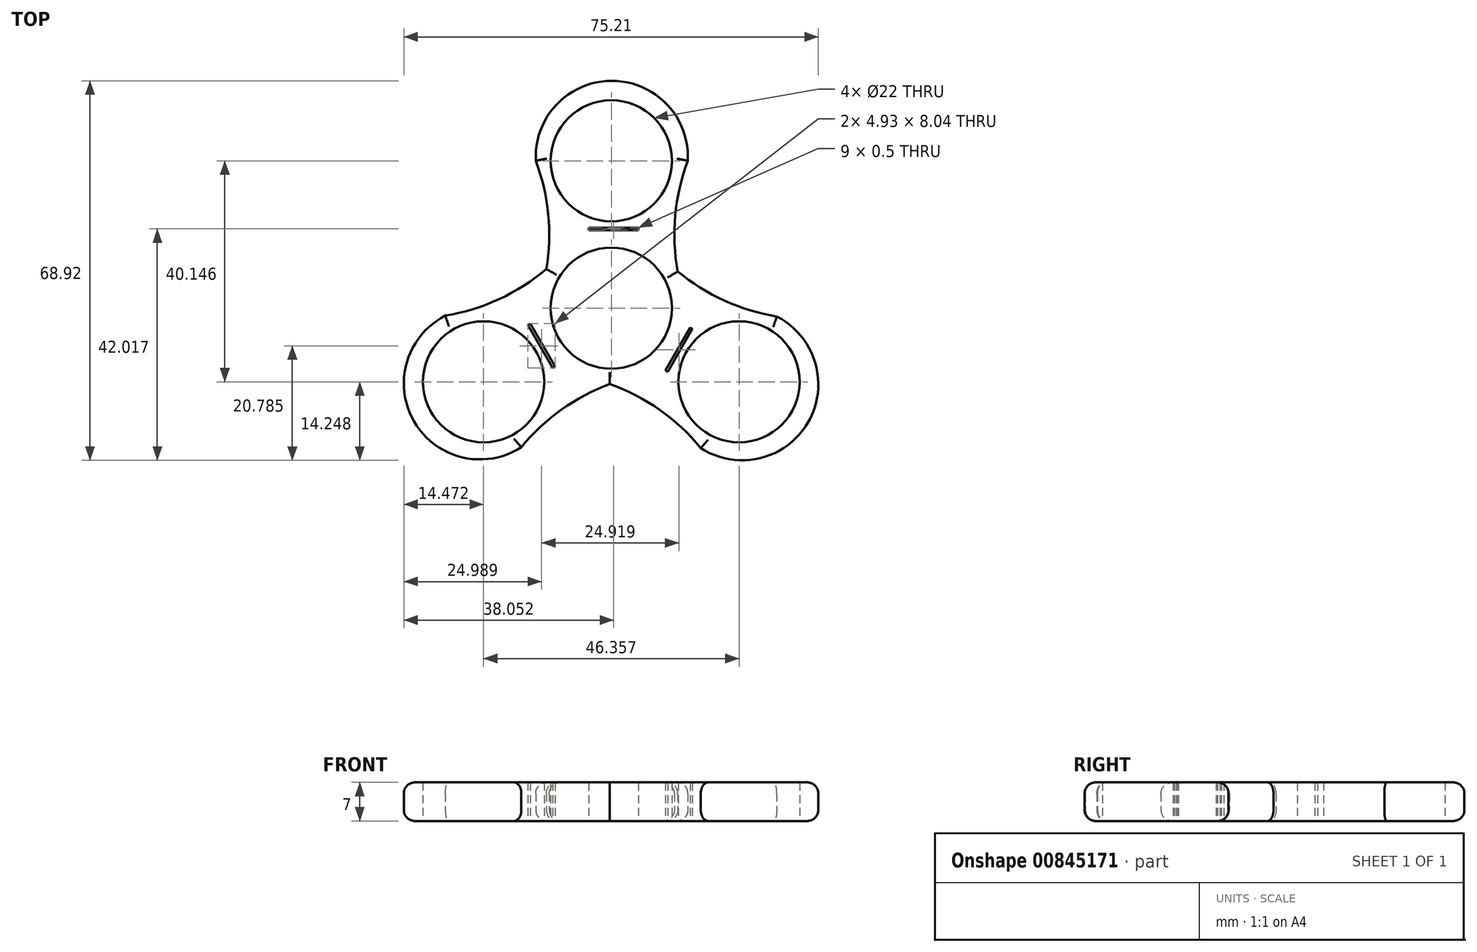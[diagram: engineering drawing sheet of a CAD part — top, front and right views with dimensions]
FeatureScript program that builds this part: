
annotation { "Feature Type Name" : "Feature", "Feature Type Description" : "" }
export const myFeature = defineFeature(function(context is Context, id is Id, definition is map)
    precondition{}
    {
        {
            var Q0;
            Q0=qCreatedBy(makeId("Top.planeOp"),FACE);
            var sketch = newSketch(context, id + "F0", { "sketchPlane" : qUnion([Q0])});
            skCircle(sketch, "E0", {"center": v(0, 0) * mm, "radius": 11 * mm});
            skCircle(sketch, "E1", {"center": v(0, 26.76) * mm, "radius": 11 * mm});
            skArc(sketch, "E2", {"start": v(13.88, 26.76) * mm, "mid": v(0.1, 41.3) * mm, "end": v(-13.7, 26.76) * mm});
            skArc(sketch, "E3", {"start": v(-13.7, 0) * mm, "mid": v(-11.27, 13.38) * mm, "end": v(-13.7, 26.76) * mm});
            skArc(sketch, "E4", {"start": v(13.88, 26.76) * mm, "mid": v(11.45, 13.38) * mm, "end": v(13.88, 0) * mm});
            skArc(sketch, "E5.1.0", {"start": v(6.85, -11.86) * mm, "mid": v(-5.96, -16.45) * mm, "end": v(-16.33, -25.25) * mm});
            skArc(sketch, "E5.1.1", {"start": v(-30.12, -1.36) * mm, "mid": v(-35.8, -20.57) * mm, "end": v(-16.33, -25.25) * mm});
            skCircle(sketch, "E5.1.2", {"center": v(-23.18, -13.38) * mm, "radius": 11 * mm});
            skArc(sketch, "E5.1.3", {"start": v(-30.12, -1.36) * mm, "mid": v(-17.31, 3.22) * mm, "end": v(-6.94, 12.02) * mm});
            skArc(sketch, "E5.2.0", {"start": v(6.85, 11.86) * mm, "mid": v(17.22, 3.07) * mm, "end": v(30.03, -1.52) * mm});
            skArc(sketch, "E5.2.1", {"start": v(16.24, -25.4) * mm, "mid": v(35.71, -20.72) * mm, "end": v(30.03, -1.52) * mm});
            skCircle(sketch, "E5.2.2", {"center": v(23.18, -13.38) * mm, "radius": 11 * mm});
            skArc(sketch, "E5.2.3", {"start": v(16.24, -25.4) * mm, "mid": v(5.87, -16.6) * mm, "end": v(-6.94, -12.02) * mm});
            skLineSegment(sketch, "E6.bottom", {"start": v(-4.1, 14.64) * mm, "end": v(4.9, 14.64) * mm});
            skLineSegment(sketch, "E6.top", {"start": v(-4.1, 14.14) * mm, "end": v(4.9, 14.14) * mm});
            skLineSegment(sketch, "E6.left", {"start": v(-4.1, 14.64) * mm, "end": v(-4.1, 14.14) * mm});
            skLineSegment(sketch, "E6.right", {"start": v(4.9, 14.64) * mm, "end": v(4.9, 14.14) * mm});
            skLineSegment(sketch, "E7.1.0", {"start": v(-10.2, -10.62) * mm, "end": v(-14.7, -2.82) * mm});
            skLineSegment(sketch, "E7.1.1", {"start": v(-10.63, -10.87) * mm, "end": v(-15.13, -3.07) * mm});
            skLineSegment(sketch, "E7.1.2", {"start": v(-10.63, -10.87) * mm, "end": v(-10.2, -10.62) * mm});
            skLineSegment(sketch, "E7.1.3", {"start": v(-15.13, -3.07) * mm, "end": v(-14.7, -2.82) * mm});
            skLineSegment(sketch, "E7.2.0", {"start": v(14.3, -3.52) * mm, "end": v(9.8, -11.32) * mm});
            skLineSegment(sketch, "E7.2.1", {"start": v(14.72, -3.77) * mm, "end": v(10.22, -11.56) * mm});
            skLineSegment(sketch, "E7.2.2", {"start": v(14.72, -3.77) * mm, "end": v(14.3, -3.52) * mm});
            skLineSegment(sketch, "E7.2.3", {"start": v(10.22, -11.56) * mm, "end": v(9.8, -11.32) * mm});
            skSolve(sketch);
        }
        {
            var Q0;
            Q0 = qSketchRegion(id + "F0", true);
            extrude(context, id + "F1", {"entities" : qUnion([Q0]), "depth" : 7 * mm, "offsetDistance" : 25 * mm});
        }
        {
            var Q0;
            Q0=makeQuery(id+"F1.opExtrude","CAP_EDGE",EDGE,{"disambiguationData":[OSD([sQuery(id+"F0.wireOp",EDGE,"E3")])],"isStart":false});
            var Q1;
            Q1=makeQuery(id+"F1.opExtrude","CAP_EDGE",EDGE,{"disambiguationData":[OSD([sQuery(id+"F0.wireOp",EDGE,"E2")])],"isStart":false});
            var Q2;
            Q2=makeQuery(id+"F1.opExtrude","CAP_EDGE",EDGE,{"disambiguationData":[OSD([sQuery(id+"F0.wireOp",EDGE,"E4")])],"isStart":false});
            var Q3;
            Q3=makeQuery(id+"F1.opExtrude","CAP_EDGE",EDGE,{"disambiguationData":[OSD([sQuery(id+"F0.wireOp",EDGE,"E5.2.0")])],"isStart":false});
            var Q4;
            Q4=makeQuery(id+"F1.opExtrude","CAP_EDGE",EDGE,{"disambiguationData":[OSD([sQuery(id+"F0.wireOp",EDGE,"E5.2.1")])],"isStart":false});
            var Q5;
            Q5=makeQuery(id+"F1.opExtrude","CAP_EDGE",EDGE,{"disambiguationData":[OSD([sQuery(id+"F0.wireOp",EDGE,"E5.2.3")])],"isStart":false});
            var Q6;
            Q6=makeQuery(id+"F1.opExtrude","CAP_EDGE",EDGE,{"disambiguationData":[OSD([sQuery(id+"F0.wireOp",EDGE,"E5.1.0")])],"isStart":false});
            var Q7;
            Q7=makeQuery(id+"F1.opExtrude","CAP_EDGE",EDGE,{"disambiguationData":[OSD([sQuery(id+"F0.wireOp",EDGE,"E5.1.1")])],"isStart":false});
            var Q8;
            Q8=makeQuery(id+"F1.opExtrude","CAP_EDGE",EDGE,{"disambiguationData":[OSD([sQuery(id+"F0.wireOp",EDGE,"E5.1.3")])],"isStart":false});
            fillet(context, id + "F2", {"entities" : qUnion([Q0, Q1, Q2, Q3, Q4, Q5, Q6, Q7, Q8]), "radius" : 2 * mm, "tangentPropagation" : true, "allowEdgeOverflow" : false});
        }
        {
            var Q0;
            Q0=makeQuery(id+"F1.opExtrude","CAP_EDGE",EDGE,{"disambiguationData":[OSD([sQuery(id+"F0.wireOp",EDGE,"E2")])],"isStart":true});
            var Q1;
            Q1=makeQuery(id+"F1.opExtrude","CAP_EDGE",EDGE,{"disambiguationData":[OSD([sQuery(id+"F0.wireOp",EDGE,"E3")])],"isStart":true});
            var Q2;
            Q2=makeQuery(id+"F1.opExtrude","CAP_EDGE",EDGE,{"disambiguationData":[OSD([sQuery(id+"F0.wireOp",EDGE,"E5.1.3")])],"isStart":true});
            var Q3;
            Q3=makeQuery(id+"F1.opExtrude","CAP_EDGE",EDGE,{"disambiguationData":[OSD([sQuery(id+"F0.wireOp",EDGE,"E5.1.1")])],"isStart":true});
            var Q4;
            Q4=makeQuery(id+"F1.opExtrude","CAP_EDGE",EDGE,{"disambiguationData":[OSD([sQuery(id+"F0.wireOp",EDGE,"E5.1.0")])],"isStart":true});
            var Q5;
            Q5=makeQuery(id+"F1.opExtrude","CAP_EDGE",EDGE,{"disambiguationData":[OSD([sQuery(id+"F0.wireOp",EDGE,"E5.2.3")])],"isStart":true});
            var Q6;
            Q6=makeQuery(id+"F1.opExtrude","CAP_EDGE",EDGE,{"disambiguationData":[OSD([sQuery(id+"F0.wireOp",EDGE,"E5.2.1")])],"isStart":true});
            var Q7;
            Q7=makeQuery(id+"F1.opExtrude","CAP_EDGE",EDGE,{"disambiguationData":[OSD([sQuery(id+"F0.wireOp",EDGE,"E5.2.0")])],"isStart":true});
            var Q8;
            Q8=makeQuery(id+"F1.opExtrude","CAP_EDGE",EDGE,{"disambiguationData":[OSD([sQuery(id+"F0.wireOp",EDGE,"E4")])],"isStart":true});
            fillet(context, id + "F3", {"entities" : qUnion([Q0, Q1, Q2, Q3, Q4, Q5, Q6, Q7, Q8]), "radius" : 2 * mm, "tangentPropagation" : true, "allowEdgeOverflow" : false});
        }
    });
